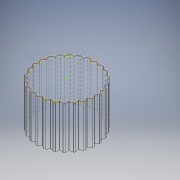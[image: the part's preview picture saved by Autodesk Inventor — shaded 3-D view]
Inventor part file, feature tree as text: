
AUTODESK INVENTOR PART (.ipt)
format: ipt  version: 2018 (Build 220112000, 112)  size: 472,064 bytes
history: native  units: mm
features: extrude x3, sketch x3, other x1, pattern_circular x1
ambient origin geometry x8: Origin, YZ Plane, XZ Plane, XY Plane, X Axis, Y Axis, Z Axis, Center Point
bodies: Solido9 (feature_tree)
feature tree (8):
  other  "<userpath>\Desktop\Cremagliera\EVOLUZ_test2.xlsx"
  extrude  "Estrusione28"  Depth=14.247139mm
  pattern_circular  "Serie circolare9"  [2 undecoded]
  extrude  "Estrusione29 diametro fondo"  Depth=13.450884mm
  extrude  "Estrusione30"  Depth=1.139832mm
  sketch  "Schizzo42"
  sketch  "Schizzo40"
  sketch  "Schizzo41"
note: 2 required parameter values undecoded (feature->parameter linkage not recoverable at this tier; creation-order binding heuristic only, values carry confidence <= 0.55)
